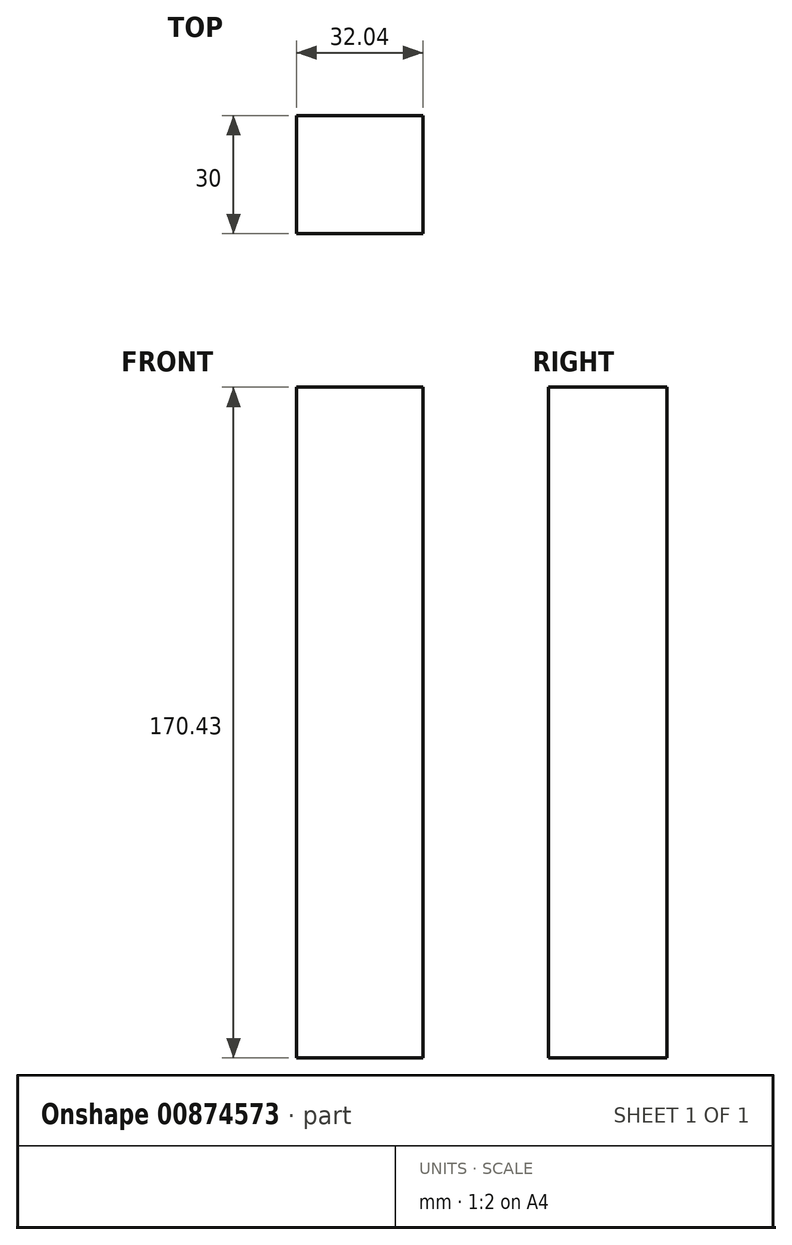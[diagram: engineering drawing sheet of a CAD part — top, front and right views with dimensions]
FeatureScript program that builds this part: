
annotation { "Feature Type Name" : "Feature", "Feature Type Description" : "" }
export const myFeature = defineFeature(function(context is Context, id is Id, definition is map)
    precondition{}
    {
        {
            var Q0;
            Q0=qCreatedBy(makeId("Top.planeOp"),FACE);
            var sketch = newSketch(context, id + "F0", { "sketchPlane" : qUnion([Q0])});
            skLineSegment(sketch, "E0.bottom", {"start": v(-17.2, 17.91) * mm, "end": v(14.84, 17.91) * mm});
            skLineSegment(sketch, "E0.top", {"start": v(-17.2, -12.09) * mm, "end": v(14.84, -12.09) * mm});
            skLineSegment(sketch, "E0.left", {"start": v(-17.2, 17.91) * mm, "end": v(-17.2, -12.09) * mm});
            skLineSegment(sketch, "E0.right", {"start": v(14.84, 17.91) * mm, "end": v(14.84, -12.09) * mm});
            skSolve(sketch);
        }
        {
            var Q0;
            Q0 = qSketchRegion(id + "F0", true);
            extrude(context, id + "F1", {"entities" : qUnion([Q0]), "depth" : 170.43 * mm, "offsetDistance" : 25.4 * mm});
        }
    });
